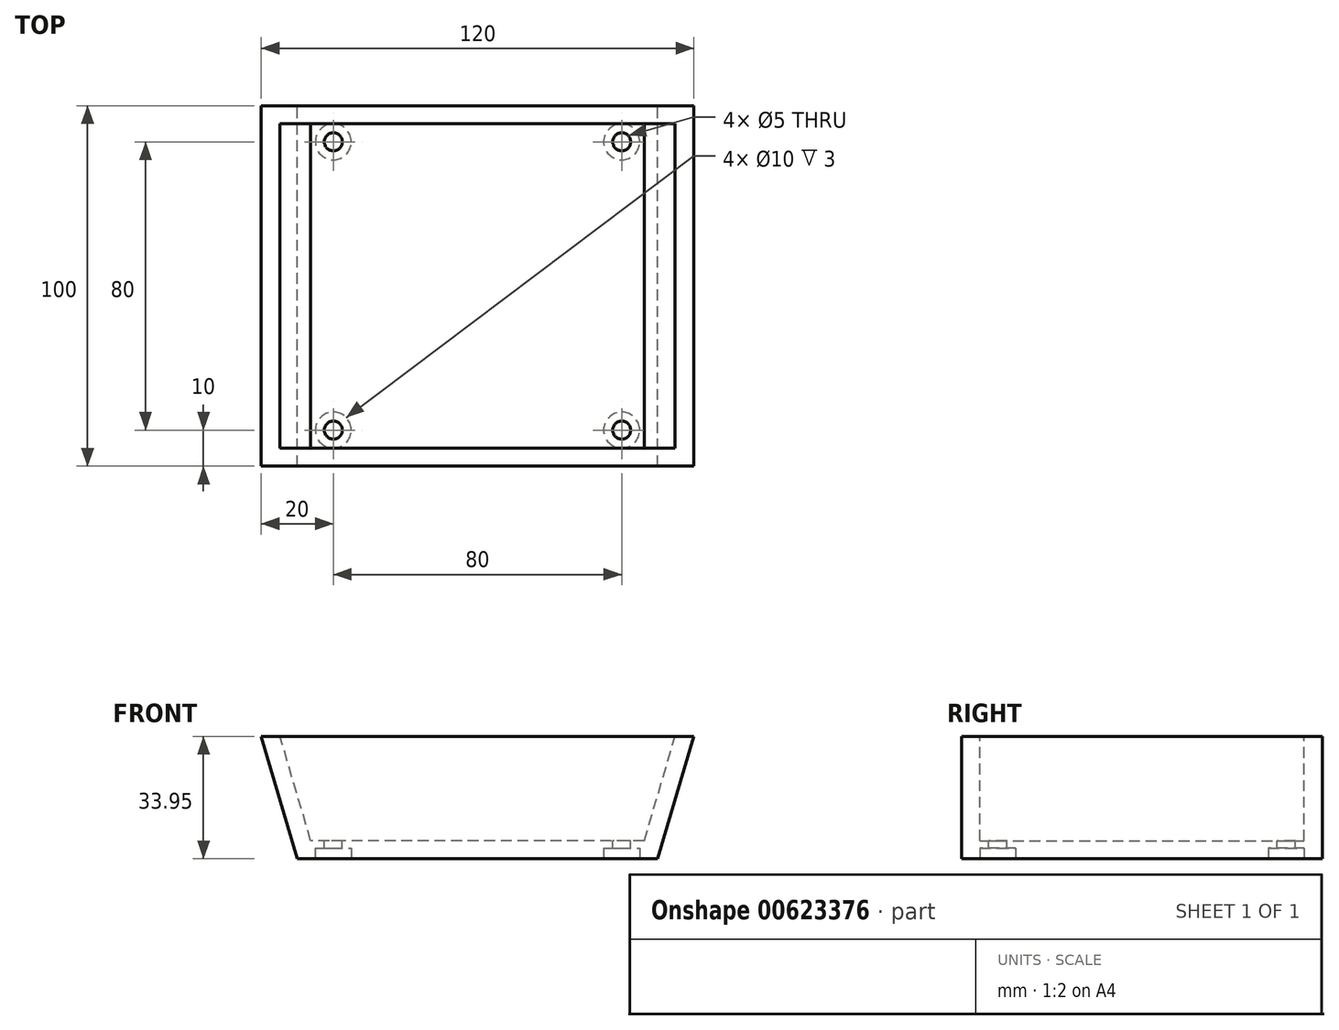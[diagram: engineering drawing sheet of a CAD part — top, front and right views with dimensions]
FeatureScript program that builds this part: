
annotation { "Feature Type Name" : "Feature", "Feature Type Description" : "" }
export const myFeature = defineFeature(function(context is Context, id is Id, definition is map)
    precondition{}
    {
        {
            var Q0;
            Q0=qCreatedBy(makeId("Front.planeOp"),FACE);
            var sketch = newSketch(context, id + "F0", { "sketchPlane" : qUnion([Q0])});
            skPoint(sketch, "E0.middle", {"position": v(0, 0) * mm});
            skLineSegment(sketch, "E1", {"start": v(50, 0) * mm, "end": v(60, 33.95) * mm});
            skLineSegment(sketch, "E2", {"start": v(50, 0) * mm, "end": v(-50, 0) * mm});
            skLineSegment(sketch, "E3", {"start": v(-50, 0) * mm, "end": v(-60, 33.95) * mm});
            skLineSegment(sketch, "E4", {"start": v(-60, 33.95) * mm, "end": v(60, 33.95) * mm});
            skPoint(sketch, "E5", {"position": v(0, 33.95) * mm});
            skSolve(sketch);
        }
        {
            var Q0;
            Q0 = qSketchRegion(id + "F0", true);
            extrude(context, id + "F1", {"entities" : qUnion([Q0]), "depth" : 50 * mm, "offsetDistance" : 25 * mm, "hasSecondDirection" : true, "secondDirectionOppositeDirection" : true, "secondDirectionDepth" : 50 * mm});
        }
        {
            var Q0;
            Q0=makeQuery(id+"F1.opExtrude","SWEPT_FACE",FACE,{"disambiguationData":[OSD([sQuery(id+"F0.wireOp",EDGE,"E4")])]});
            shell(context, id + "F2", {"entities" : qUnion([Q0]), "thickness" : 5 * mm});
        }
        {
            var Q0;
            Q0=makeQuery(id+"F2.opShell","OFFSET_FACE",FACE,{"disambiguationData":[OSD([sQuery(id+"F0.wireOp",EDGE,"E2")])]});
            var sketch = newSketch(context, id + "F3", { "sketchPlane" : qUnion([Q0])});
            skCircle(sketch, "E6", {"center": v(-40, 40) * mm, "radius": 2.5 * mm});
            skCircle(sketch, "E7.1.0", {"center": v(-40, -40) * mm, "radius": 2.5 * mm});
            skCircle(sketch, "E7.2.0", {"center": v(40, -40) * mm, "radius": 2.5 * mm});
            skCircle(sketch, "E7.3.0", {"center": v(40, 40) * mm, "radius": 2.5 * mm});
            skPoint(sketch, "E7.center", {"position": v(0, 0) * mm});
            skSolve(sketch);
        }
        {
            var Q0;
            Q0 = qSketchRegion(id + "F3", true);
            extrude(context, id + "F4", {"entities" : qUnion([Q0]), "operationType" : NewBodyOperationType.REMOVE, "endBound" : BoundingType.UP_TO_NEXT, "oppositeDirection" : true, "depth" : 25 * mm, "offsetDistance" : 25 * mm});
        }
        {
            var Q0;
            Q0=makeQuery(id+"F1.opExtrude","SWEPT_FACE",FACE,{"disambiguationData":[OSD([sQuery(id+"F0.wireOp",EDGE,"E2")])]});
            var sketch = newSketch(context, id + "F5", { "sketchPlane" : qUnion([Q0])});
            skCircle(sketch, "E8", {"center": v(-40, 40) * mm, "radius": 5 * mm});
            skCircle(sketch, "E9.1.0", {"center": v(40, 40) * mm, "radius": 5 * mm});
            skCircle(sketch, "E9.2.0", {"center": v(40, -40) * mm, "radius": 5 * mm});
            skCircle(sketch, "E9.3.0", {"center": v(-40, -40) * mm, "radius": 5 * mm});
            skPoint(sketch, "E9.center", {"position": v(0, 0) * mm});
            skLineSegment(sketch, "E9.anchor1", {"start": v(0, 0) * mm, "end": v(-40, 40) * mm, "construction": true});
            skLineSegment(sketch, "E9.anchor2", {"start": v(0, 0) * mm, "end": v(-40, -40) * mm, "construction": true});
            skSolve(sketch);
        }
        {
            var Q0;
            Q0=makeQuery(id+"F5.imprint","IMPRINT",FACE,{"disambiguationData":[TD([[makeQuery(id+"F5.imprint","IMPRINT",EDGE,{"derivedFrom":sQuery(id+"F5.wireOp",EDGE,"E8")}),1.0]])]});
            var Q1;
            Q1=makeQuery(id+"F5.imprint","IMPRINT",FACE,{"disambiguationData":[TD([[makeQuery(id+"F5.imprint","IMPRINT",EDGE,{"derivedFrom":sQuery(id+"F5.wireOp",EDGE,"E9.1.0")}),1.0]])]});
            var Q2;
            Q2=makeQuery(id+"F5.imprint","IMPRINT",FACE,{"disambiguationData":[TD([[makeQuery(id+"F5.imprint","IMPRINT",EDGE,{"derivedFrom":sQuery(id+"F5.wireOp",EDGE,"E9.2.0")}),1.0]])]});
            var Q3;
            Q3=makeQuery(id+"F5.imprint","IMPRINT",FACE,{"disambiguationData":[TD([[makeQuery(id+"F5.imprint","IMPRINT",EDGE,{"derivedFrom":sQuery(id+"F5.wireOp",EDGE,"E9.3.0")}),1.0]])]});
            var Q4;
            Q4=sQuery(id+"F5.wireOp",EDGE,"E9.1.0");
            extrude(context, id + "F6", {"entities" : qUnion([Q0, Q1, Q2, Q3]), "operationType" : NewBodyOperationType.REMOVE, "surfaceEntities" : qUnion([Q4]), "oppositeDirection" : true, "depth" : 3 * mm, "offsetDistance" : 25 * mm});
        }
    });
